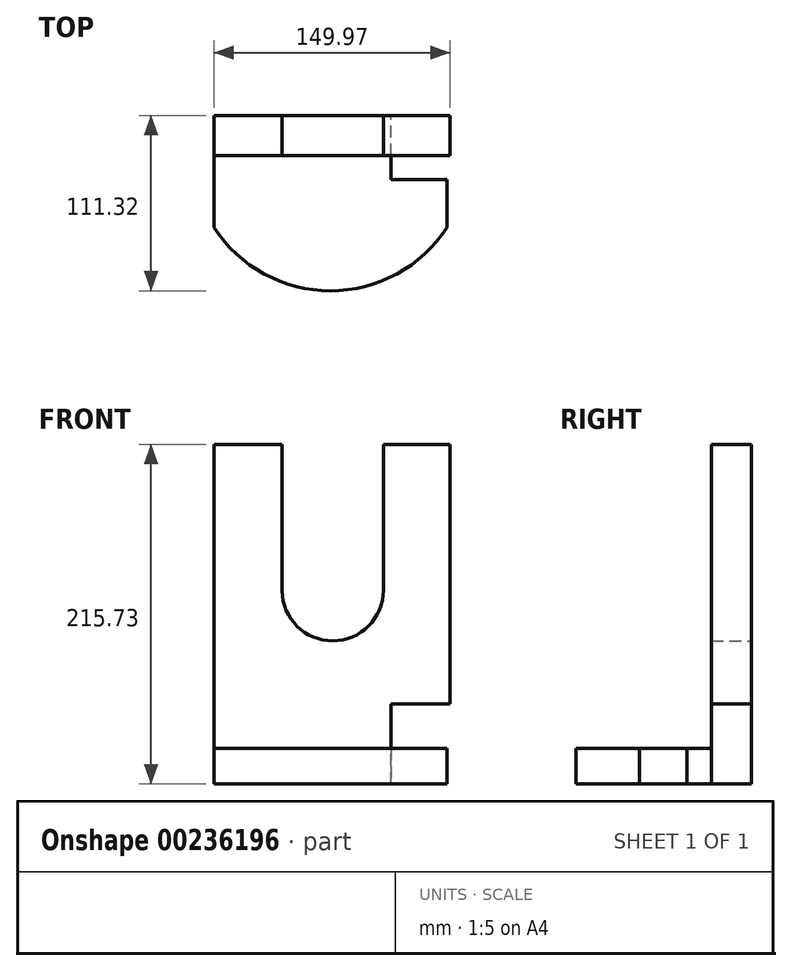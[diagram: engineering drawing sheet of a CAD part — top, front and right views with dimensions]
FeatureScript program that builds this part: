
annotation { "Feature Type Name" : "Feature", "Feature Type Description" : "" }
export const myFeature = defineFeature(function(context is Context, id is Id, definition is map)
    precondition{}
    {
        {
            var Q0;
            Q0=qCreatedBy(makeId("Front.planeOp"),FACE);
            var sketch = newSketch(context, id + "F0", { "sketchPlane" : qUnion([Q0])});
            skLineSegment(sketch, "E0.bottom", {"start": v(-38.54, 101.66) * mm, "end": v(4.65, 101.66) * mm});
            skLineSegment(sketch, "E0.top", {"start": v(-38.54, -114.07) * mm, "end": v(73.82, -114.07) * mm});
            skLineSegment(sketch, "E0.left", {"start": v(-38.54, 101.66) * mm, "end": v(-38.54, -114.07) * mm});
            skLineSegment(sketch, "E0.right", {"start": v(111.43, 101.66) * mm, "end": v(111.43, -63.35) * mm});
            skLineSegment(sketch, "E1", {"start": v(4.65, 101.66) * mm, "end": v(4.65, 8.72) * mm});
            skLineSegment(sketch, "E2", {"start": v(68.96, 101.66) * mm, "end": v(68.96, 8.96) * mm});
            skArc(sketch, "E3", {"start": v(4.65, 8.72) * mm, "mid": v(36.93, -23.2) * mm, "end": v(68.96, 8.96) * mm});
            skLineSegment(sketch, "E4.trimOffspring", {"start": v(68.96, 101.66) * mm, "end": v(111.43, 101.66) * mm});
            skLineSegment(sketch, "E5", {"start": v(111.43, -63.35) * mm, "end": v(73.82, -63.35) * mm});
            skLineSegment(sketch, "E6", {"start": v(73.82, -63.35) * mm, "end": v(73.82, -114.07) * mm});
            skSolve(sketch);
        }
        {
            var Q0;
            Q0 = qSketchRegion(id + "F0", true);
            extrude(context, id + "F1", {"entities" : qUnion([Q0]), "depth" : 25.4 * mm});
        }
        {
            var Q0;
            Q0=makeQuery(id+"F1.opExtrude","SWEPT_FACE",FACE,{"disambiguationData":[OSD([sQuery(id+"F0.wireOp",EDGE,"E0.top")])]});
            var sketch = newSketch(context, id + "F2", { "sketchPlane" : qUnion([Q0])});
            skLineSegment(sketch, "E7.bottom", {"start": v(-38.54, 0) * mm, "end": v(73.7, 0) * mm});
            skLineSegment(sketch, "E7.left", {"start": v(-38.54, 0) * mm, "end": v(-38.54, 71.04) * mm});
            skLineSegment(sketch, "E7.right", {"start": v(73.7, 0) * mm, "end": v(73.7, 40.8) * mm});
            skLineSegment(sketch, "E8.top", {"start": v(73.7, 40.8) * mm, "end": v(109.37, 40.8) * mm});
            skLineSegment(sketch, "E8.right", {"start": v(109.37, 71.04) * mm, "end": v(109.37, 40.8) * mm});
            skArc(sketch, "E9", {"start": v(109.37, 71.04) * mm, "mid": v(35.41, 111.32) * mm, "end": v(-38.54, 71.04) * mm});
            skSolve(sketch);
        }
        {
            var Q0;
            Q0 = qSketchRegion(id + "F2", true);
            extrude(context, id + "F3", {"entities" : qUnion([Q0]), "operationType" : NewBodyOperationType.ADD, "oppositeDirection" : true, "depth" : 22.6 * mm});
        }
    });
